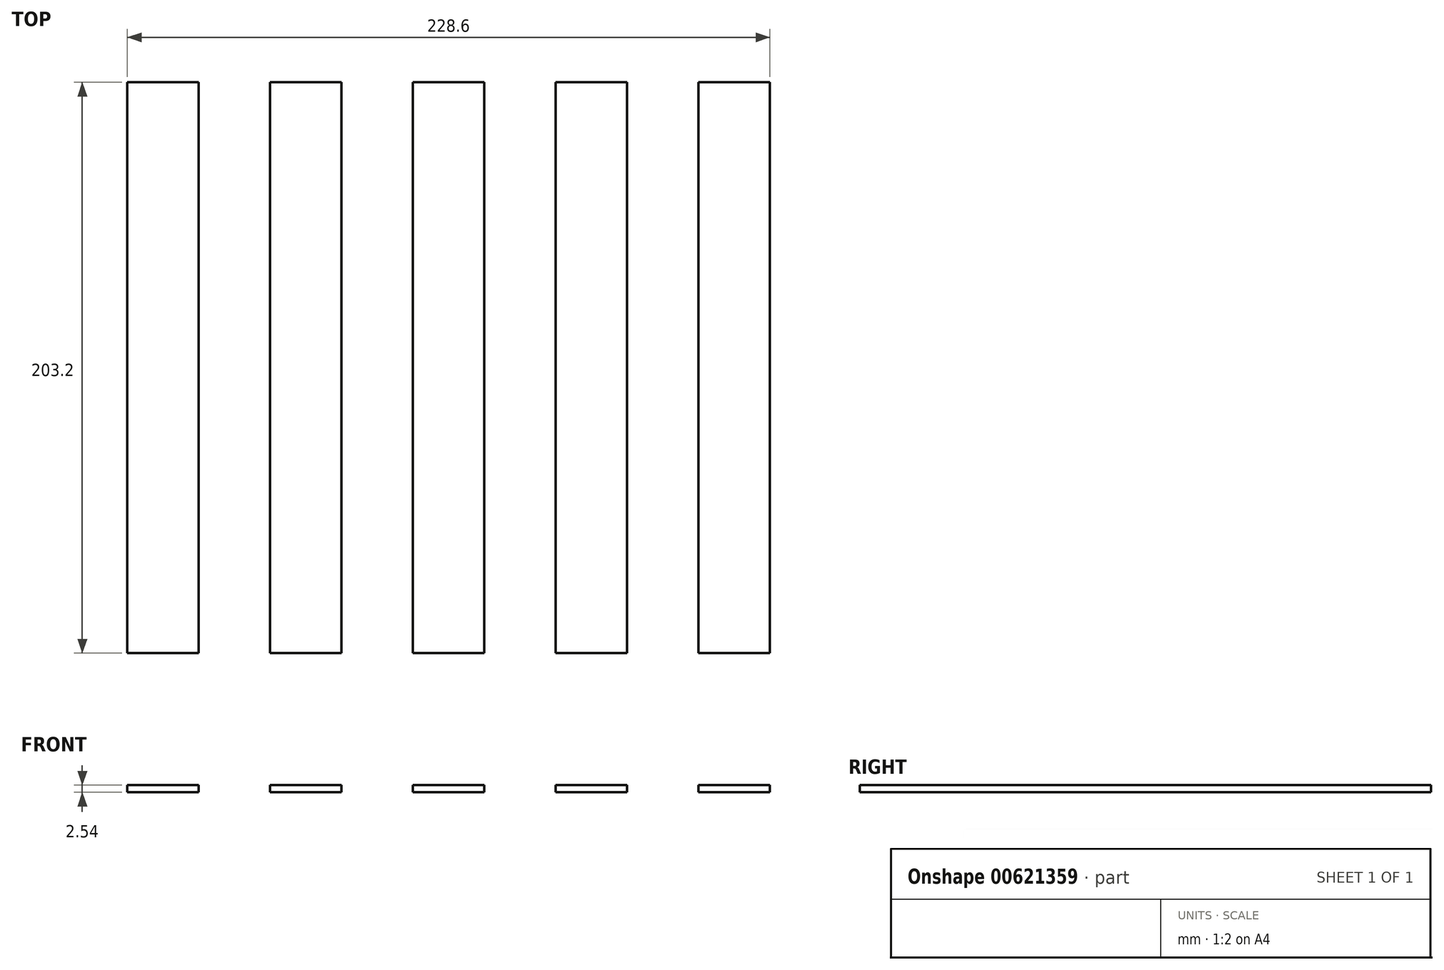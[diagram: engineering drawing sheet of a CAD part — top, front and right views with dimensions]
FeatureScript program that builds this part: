
annotation { "Feature Type Name" : "Feature", "Feature Type Description" : "" }
export const myFeature = defineFeature(function(context is Context, id is Id, definition is map)
    precondition{}
    {
        {
            var Q0;
            Q0=qCreatedBy(makeId("Top.planeOp"),FACE);
            var sketch = newSketch(context, id + "F0", { "sketchPlane" : qUnion([Q0])});
            skLineSegment(sketch, "E0", {"start": v(0, 0) * mm, "end": v(25.4, 0) * mm});
            skLineSegment(sketch, "E1", {"start": v(25.4, 0) * mm, "end": v(50.8, 0) * mm});
            skLineSegment(sketch, "E2", {"start": v(50.8, 0) * mm, "end": v(76.2, 0) * mm});
            skLineSegment(sketch, "E3", {"start": v(76.2, 0) * mm, "end": v(101.6, 0) * mm});
            skLineSegment(sketch, "E4", {"start": v(101.6, 0) * mm, "end": v(127, 0) * mm});
            skLineSegment(sketch, "E5", {"start": v(127, 0) * mm, "end": v(152.4, 0) * mm});
            skPoint(sketch, "E5.endSnap0", {"position": v(114.3, 0) * mm});
            skLineSegment(sketch, "E6", {"start": v(152.4, 0) * mm, "end": v(177.8, 0) * mm});
            skLineSegment(sketch, "E7", {"start": v(177.8, 0) * mm, "end": v(203.2, 0) * mm});
            skLineSegment(sketch, "E8", {"start": v(203.2, 0) * mm, "end": v(228.6, 0) * mm});
            skLineSegment(sketch, "E9", {"start": v(228.6, 0) * mm, "end": v(254, 0) * mm});
            skLineSegment(sketch, "E10", {"start": v(254, 0) * mm, "end": v(254, 25.4) * mm});
            skLineSegment(sketch, "E11", {"start": v(254, 25.4) * mm, "end": v(254, 50.8) * mm});
            skLineSegment(sketch, "E12", {"start": v(254, 50.8) * mm, "end": v(254, 76.2) * mm});
            skLineSegment(sketch, "E13", {"start": v(254, 76.2) * mm, "end": v(254, 101.6) * mm});
            skLineSegment(sketch, "E14", {"start": v(254, 101.6) * mm, "end": v(254, 127) * mm});
            skLineSegment(sketch, "E15", {"start": v(254, 127) * mm, "end": v(254, 152.4) * mm});
            skLineSegment(sketch, "E16", {"start": v(254, 152.4) * mm, "end": v(254, 177.8) * mm});
            skLineSegment(sketch, "E17", {"start": v(254, 177.8) * mm, "end": v(254, 203.2) * mm});
            skLineSegment(sketch, "E18", {"start": v(254, 203.2) * mm, "end": v(0, 203.2) * mm});
            skLineSegment(sketch, "E19", {"start": v(0, 203.2) * mm, "end": v(0, 0) * mm});
            skLineSegment(sketch, "E20", {"start": v(25.4, 0) * mm, "end": v(25.4, 203.2) * mm});
            skLineSegment(sketch, "E21", {"start": v(50.8, 0) * mm, "end": v(50.8, 203.2) * mm});
            skLineSegment(sketch, "E22", {"start": v(76.2, 0) * mm, "end": v(76.2, 203.2) * mm});
            skLineSegment(sketch, "E23", {"start": v(101.6, 0) * mm, "end": v(101.6, 203.2) * mm});
            skLineSegment(sketch, "E24", {"start": v(127, 0) * mm, "end": v(127, 203.2) * mm});
            skLineSegment(sketch, "E25", {"start": v(152.4, 0) * mm, "end": v(152.4, 203.2) * mm});
            skLineSegment(sketch, "E26", {"start": v(177.8, 0) * mm, "end": v(177.8, 203.2) * mm});
            skLineSegment(sketch, "E27", {"start": v(203.2, 0) * mm, "end": v(203.2, 203.2) * mm});
            skLineSegment(sketch, "E28", {"start": v(228.6, 0) * mm, "end": v(228.6, 203.2) * mm});
            skSolve(sketch);
        }
        {
            var Q0;
            Q0=makeQuery(id+"F0.imprint","IMPRINT",FACE,{"disambiguationData":[TD([[makeQuery(id+"F0.imprint","IMPRINT",EDGE,{"derivedFrom":sQuery(id+"F0.wireOp",EDGE,"E0")}),1.0]])]});
            var Q1;
            Q1=makeQuery(id+"F0.imprint","IMPRINT",FACE,{"disambiguationData":[TD([[makeQuery(id+"F0.imprint","IMPRINT",EDGE,{"derivedFrom":sQuery(id+"F0.wireOp",EDGE,"E2")}),1.0]])]});
            var Q2;
            Q2=makeQuery(id+"F0.imprint","IMPRINT",FACE,{"disambiguationData":[TD([[makeQuery(id+"F0.imprint","IMPRINT",EDGE,{"derivedFrom":sQuery(id+"F0.wireOp",EDGE,"E4")}),1.0]])]});
            var Q3;
            Q3=makeQuery(id+"F0.imprint","IMPRINT",FACE,{"disambiguationData":[TD([[makeQuery(id+"F0.imprint","IMPRINT",EDGE,{"derivedFrom":sQuery(id+"F0.wireOp",EDGE,"E6")}),1.0]])]});
            var Q4;
            Q4=makeQuery(id+"F0.imprint","IMPRINT",FACE,{"disambiguationData":[TD([[makeQuery(id+"F0.imprint","IMPRINT",EDGE,{"derivedFrom":sQuery(id+"F0.wireOp",EDGE,"E8")}),1.0]])]});
            extrude(context, id + "F1", {"entities" : qUnion([Q0, Q1, Q2, Q3, Q4]), "depth" : 2.54 * mm, "offsetDistance" : 25.4 * mm});
        }
    });
